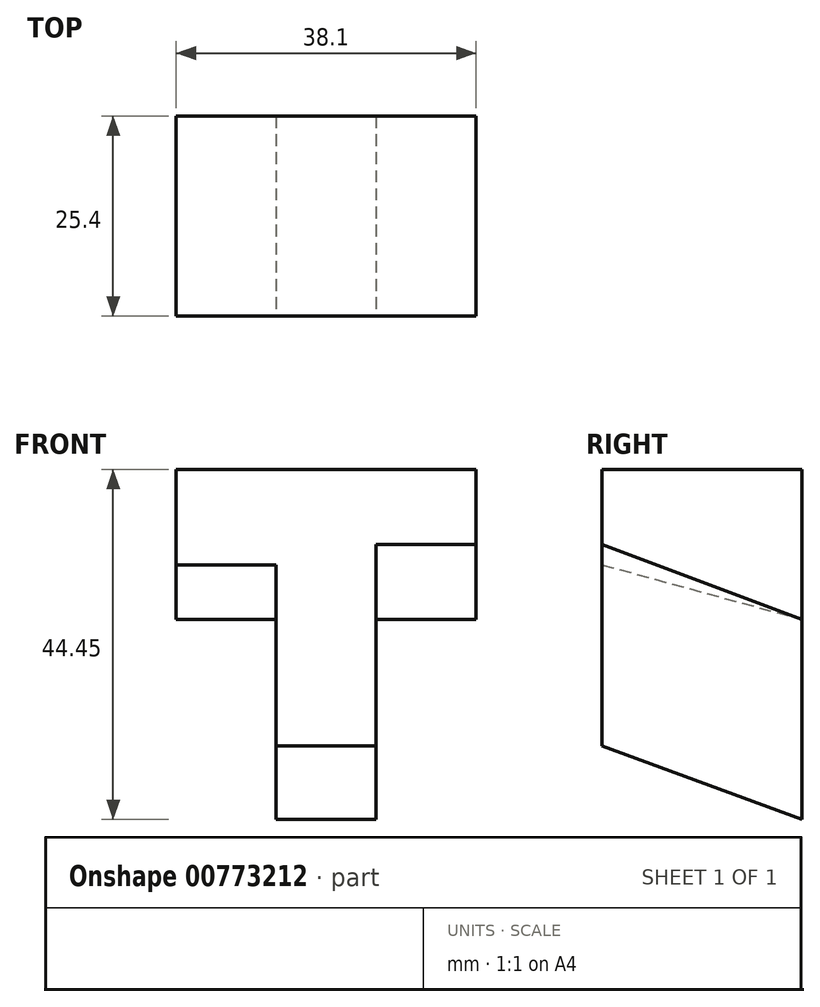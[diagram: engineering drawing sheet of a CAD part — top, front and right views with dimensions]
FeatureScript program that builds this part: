
annotation { "Feature Type Name" : "Feature", "Feature Type Description" : "" }
export const myFeature = defineFeature(function(context is Context, id is Id, definition is map)
    precondition{}
    {
        {
            var Q0;
            Q0=qCreatedBy(makeId("Front.planeOp"),FACE);
            var sketch = newSketch(context, id + "F0", { "sketchPlane" : qUnion([Q0])});
            skLineSegment(sketch, "E0", {"start": v(0, 25.4) * mm, "end": v(0, 0) * mm});
            skLineSegment(sketch, "E1", {"start": v(0, 0) * mm, "end": v(12.7, 0) * mm});
            skLineSegment(sketch, "E2", {"start": v(12.7, 0) * mm, "end": v(12.7, 25.4) * mm});
            skLineSegment(sketch, "E3", {"start": v(12.7, 25.4) * mm, "end": v(25.4, 25.4) * mm});
            skLineSegment(sketch, "E4", {"start": v(25.4, 25.4) * mm, "end": v(25.4, 44.45) * mm});
            skLineSegment(sketch, "E5", {"start": v(25.4, 44.45) * mm, "end": v(-12.7, 44.45) * mm});
            skLineSegment(sketch, "E6", {"start": v(-12.7, 44.45) * mm, "end": v(-12.7, 25.4) * mm});
            skLineSegment(sketch, "E7", {"start": v(-12.7, 25.4) * mm, "end": v(0, 25.4) * mm});
            skSolve(sketch);
        }
        {
            var Q0;
            Q0 = qSketchRegion(id + "F0", true);
            extrude(context, id + "F1", {"entities" : qUnion([Q0]), "depth" : 25.4 * mm, "offsetDistance" : 25.4 * mm});
        }
        {
            var Q0;
            Q0=makeQuery(id+"F1.opExtrude","SWEPT_FACE",FACE,{"disambiguationData":[OSD([sQuery(id+"F0.wireOp",EDGE,"E0")])]});
            var sketch = newSketch(context, id + "F2", { "sketchPlane" : qUnion([Q0])});
            skLineSegment(sketch, "E8", {"start": v(0, 0) * mm, "end": v(25.4, 9.34) * mm});
            skSolve(sketch);
        }
        {
            var Q0;
            Q0 = qSketchRegion(id + "F2", true);
            var Q1;
            {var subQ0=sQuery(id+"F2.wireOp",EDGE,"E8");Q1=makeQuery(id+"F2.imprint","IMPRINT",FACE,{"disambiguationData":[TD([[makeQuery(id+"F2.imprint","IMPRINT",EDGE,{"derivedFrom":subQ0}),-1.0]])]});}
            extrude(context, id + "F3", {"entities" : qUnion([Q0, Q1]), "operationType" : NewBodyOperationType.REMOVE, "oppositeDirection" : true, "depth" : 25.4 * mm, "offsetDistance" : 25.4 * mm});
        }
        {
            var Q0;
            Q0=makeQuery(id+"F1.opExtrude","SWEPT_FACE",FACE,{"disambiguationData":[OSD([sQuery(id+"F0.wireOp",EDGE,"E6")])]});
            var sketch = newSketch(context, id + "F4", { "sketchPlane" : qUnion([Q0])});
            skLineSegment(sketch, "E9", {"start": v(25.4, 32.35) * mm, "end": v(0, 25.4) * mm});
            skSolve(sketch);
        }
        {
            var Q0;
            Q0 = qSketchRegion(id + "F4", true);
            var Q1;
            {var subQ0=sQuery(id+"F4.wireOp",EDGE,"E9");Q1=makeQuery(id+"F4.imprint","IMPRINT",FACE,{"disambiguationData":[TD([[makeQuery(id+"F4.imprint","IMPRINT",EDGE,{"derivedFrom":subQ0}),1.0]])]});}
            extrude(context, id + "F5", {"entities" : qUnion([Q0, Q1]), "operationType" : NewBodyOperationType.REMOVE, "oppositeDirection" : true, "depth" : 12.7 * mm, "offsetDistance" : 25.4 * mm});
        }
        {
            var Q0;
            Q0=makeQuery(id+"F1.opExtrude","SWEPT_FACE",FACE,{"disambiguationData":[OSD([sQuery(id+"F0.wireOp",EDGE,"E4")])]});
            var sketch = newSketch(context, id + "F6", { "sketchPlane" : qUnion([Q0])});
            skLineSegment(sketch, "E10", {"start": v(0, 25.4) * mm, "end": v(-25.4, 34.92) * mm});
            skSolve(sketch);
        }
        {
            var Q0;
            {var subQ0=sQuery(id+"F6.wireOp",EDGE,"E10");Q0=makeQuery(id+"F6.imprint","IMPRINT",FACE,{"disambiguationData":[TD([[makeQuery(id+"F6.imprint","IMPRINT",EDGE,{"derivedFrom":subQ0}),1.0]])]});}
            extrude(context, id + "F7", {"entities" : qUnion([Q0]), "operationType" : NewBodyOperationType.REMOVE, "oppositeDirection" : true, "depth" : 12.7 * mm, "offsetDistance" : 25.4 * mm});
        }
    });
